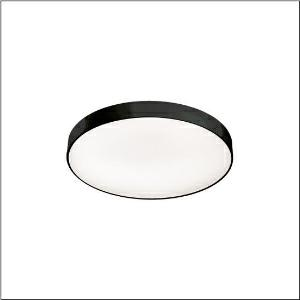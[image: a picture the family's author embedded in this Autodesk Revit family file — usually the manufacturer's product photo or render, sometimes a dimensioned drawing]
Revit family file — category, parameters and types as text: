
# Revit family: round_21_m_51mr36nd0321b
name_source: partatom
category: Lighting Fixtures
units: mm (PartAtom-declared; Revit-internal decimal feet)

## family parameters
Cut with Voids When Loaded = No
Host = Face
Light Source = No
Part Type = Normal
Room Calculation Point = No
Round Connector Dimension = Use Diameter
Shared = No

## types (1)
- Round 21 M (1 x LED, 7170 lm, 54.6 W, 3000K)
    Apparent Load = 55 VA
    CIE Flux Codes = 66 90 98 84 100
    Color Rendering = 80
    Color Temperature = 3000K
    Default Elevation = 1800 mm
    Description = Round 21 M, wall and ceiling luminaire, primary optical cover: micro prismatic cover, of PMMA, transparent, CAT 2 (L<= 3000cd/m²), light emission: direct/indirect distribution, primary light characteristic: symmetric, installation type: surface-mounted, suspended mounting, LED, rated luminous flux: 7.130lm, luminous efficacy: 131lm/W, light colour: 830, colour temperature: 3000K, control gear: DALI 2, with terminal, 5-pole, mains connection: 230V, AC, 50/60Hz, rated input power: 54.6W, housing, of aluminium, coated, black, diameter: 600mm, height: 62mm, protection rating (complete): IP40, insulation class (complete): insulation class I (protective earthing), certification: CE, impact resistance: IK04, permissible operating ambient temperature: -10..+35°C, packaging unit: 1 piece
    Height = 87 mm
    Lamp = 1 x LED
    Lamp Light Flux = 7170 lm
    Lamp Power = 54.6 W
    Lamp count = 1
    Length = 600 mm
    Luminous efficacy = 131 lm/W
    Manufacturer = Siteco
    ModVariant = No
    Model = 51MR36ND0321B
    Mounting Place = Ceiling
    Mounting Type = Surface mounted
    Number of Poles = 1
    OnlyDefault = Yes
    Power Factor = 1
    Product Name = Round 21 M
    Product group = wall and ceiling luminaire | ceiling mounted
    ProductGroupID = 304
    Protection Class = Protection class I
    Protection Degree = IP 40
    RLX_Detail_Level = 1
    RLX_Emergency_Light_Flux = 0 lm
    RLX_Emergency_Type = 0
    RLX_Emergency_Type_DB = No
    RlxData = <blob elided: 21965 chars, md5=d1b40397>
    Socket = socket
    Standby Power = 0 W
    System Light Flux = 7170 lm
    System Power = 55 W
    Type Comments = Product without accessories
    Type Image = l_1258305.jpg
    URL = http://relux.com
    VarID = ---
    Voltage = 0 V
    Weight = 0.00 kg
    Width = 0 mm  [stored 0 ft]

note: [stored X ft] marks values corroborated as IEEE doubles in the binary element streams (Revit-internal decimal feet)

## geometry (parser evidence)
native form markers: Blend x4, Sweep x11
no freeform markers — native parametric forms only
